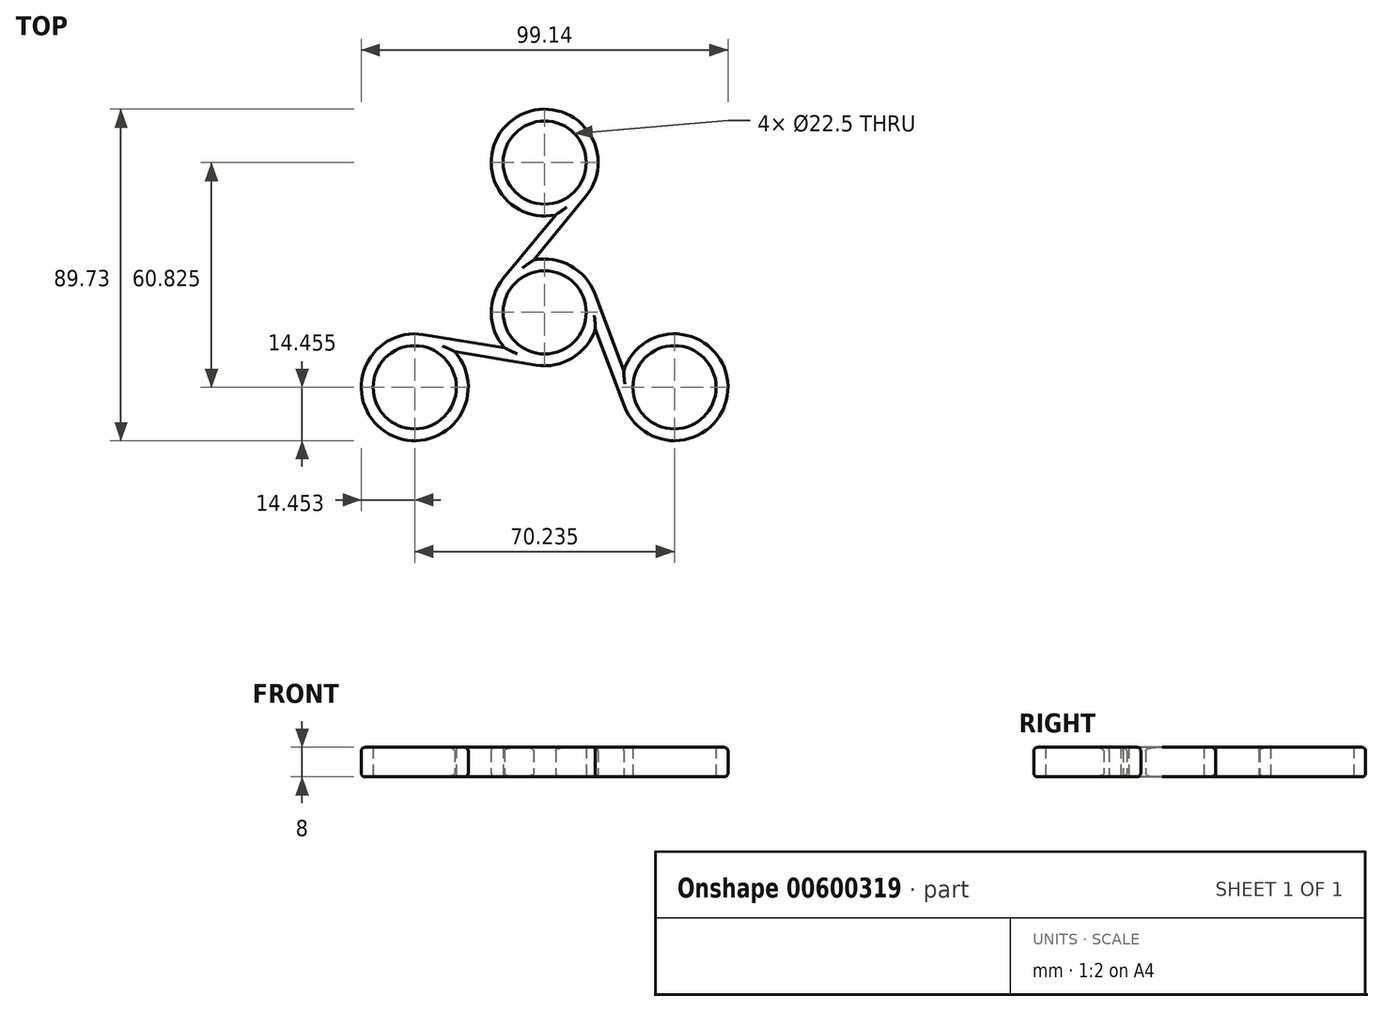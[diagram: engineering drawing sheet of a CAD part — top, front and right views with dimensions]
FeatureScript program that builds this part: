
annotation { "Feature Type Name" : "Feature", "Feature Type Description" : "" }
export const myFeature = defineFeature(function(context is Context, id is Id, definition is map)
    precondition{}
    {
        {
            var Q0;
            Q0=qCreatedBy(makeId("Top.planeOp"),FACE);
            var sketch = newSketch(context, id + "F0", { "sketchPlane" : qUnion([Q0])});
            skCircle(sketch, "E0", {"center": v(0, 0) * mm, "radius": 11.25 * mm});
            skLineSegment(sketch, "E1", {"start": v(0, 0) * mm, "end": v(0, 40.55) * mm, "construction": true});
            skLineSegment(sketch, "E2", {"start": v(-35.12, -20.27) * mm, "end": v(0, 0) * mm, "construction": true});
            skLineSegment(sketch, "E3", {"start": v(0, 0) * mm, "end": v(35.12, -20.27) * mm, "construction": true});
            skCircle(sketch, "E4", {"center": v(0, 40.55) * mm, "radius": 11.25 * mm});
            skCircle(sketch, "E5", {"center": v(35.12, -20.27) * mm, "radius": 11.25 * mm});
            skCircle(sketch, "E6", {"center": v(-35.12, -20.27) * mm, "radius": 11.25 * mm});
            skCircle(sketch, "E7", {"center": v(0, 0) * mm, "radius": 55 * mm, "construction": true});
            skCircle(sketch, "E8", {"center": v(0, 0) * mm, "radius": 14.45 * mm});
            skLineSegment(sketch, "E9", {"start": v(10.53, 3.97) * mm, "end": v(21.6, -25.38) * mm});
            skLineSegment(sketch, "E10", {"start": v(13.52, 5.1) * mm, "end": v(24.6, -24.25) * mm});
            skCircle(sketch, "E11", {"center": v(35.12, -20.27) * mm, "radius": 14.45 * mm});
            skCircle(sketch, "E12", {"center": v(0, 40.55) * mm, "radius": 14.45 * mm});
            skCircle(sketch, "E13", {"center": v(-35.12, -20.27) * mm, "radius": 14.45 * mm});
            skLineSegment(sketch, "E14", {"start": v(-1.82, -11.1) * mm, "end": v(-32.77, -6.02) * mm});
            skLineSegment(sketch, "E15", {"start": v(-2.34, -14.26) * mm, "end": v(-33.3, -9.17) * mm});
            skLineSegment(sketch, "E16", {"start": v(-11.18, 9.16) * mm, "end": v(8.7, 33.42) * mm});
            skLineSegment(sketch, "E17", {"start": v(11.18, 31.4) * mm, "end": v(-8.7, 7.13) * mm});
            skSolve(sketch);
        }
        {
            var Q0;
            Q0 = qSketchRegion(id + "F0", true);
            extrude(context, id + "F1", {"entities" : qUnion([Q0]), "endBound" : BoundingType.SYMMETRIC, "depth" : 8 * mm, "offsetDistance" : 25 * mm});
        }
        {
            var Q0;
            {var subQ0=sQuery(id+"F0.wireOp",EDGE,"E8");Q0=makeQuery(id+"F1.opExtrude","CAP_EDGE",EDGE,{"disambiguationData":[OSD([subQ0]),TDD([makeQuery(id+"F0.imprint","IMPRINT",EDGE,{"disambiguationData":[TD([[makeQuery(id+"F0.imprint","INTERSECT",VERTEX,{"derivedFrom":[subQ0,sQuery(id+"F0.wireOp",EDGE,"E10")]}),-1.0]])],"derivedFrom":subQ0})])],"isStart":false});}
            var Q1;
            Q1=makeQuery(id+"F1.opExtrude","CAP_EDGE",EDGE,{"disambiguationData":[OSD([sQuery(id+"F0.wireOp",EDGE,"E11")])],"isStart":false});
            var Q2;
            Q2=makeQuery(id+"F1.opExtrude","CAP_EDGE",EDGE,{"disambiguationData":[OSD([sQuery(id+"F0.wireOp",EDGE,"E12")])],"isStart":false});
            var Q3;
            Q3=makeQuery(id+"F1.opExtrude","CAP_EDGE",EDGE,{"disambiguationData":[OSD([sQuery(id+"F0.wireOp",EDGE,"E16")])],"isStart":false});
            var Q4;
            Q4=makeQuery(id+"F1.opExtrude","CAP_EDGE",EDGE,{"disambiguationData":[OSD([sQuery(id+"F0.wireOp",EDGE,"E13")])],"isStart":false});
            var Q5;
            {var subQ0=sQuery(id+"F0.wireOp",EDGE,"E8");Q5=makeQuery(id+"F1.opExtrude","CAP_EDGE",EDGE,{"disambiguationData":[OSD([subQ0]),TDD([makeQuery(id+"F0.imprint","IMPRINT",EDGE,{"disambiguationData":[TD([[makeQuery(id+"F0.imprint","INTERSECT",VERTEX,{"derivedFrom":[subQ0,sQuery(id+"F0.wireOp",EDGE,"E15")]}),-1.0]])],"derivedFrom":subQ0})])],"isStart":false});}
            var Q6;
            Q6=makeQuery(id+"F1.opExtrude","CAP_EDGE",EDGE,{"disambiguationData":[OSD([sQuery(id+"F0.wireOp",EDGE,"E15")])],"isStart":false});
            var Q7;
            Q7=makeQuery(id+"F1.opExtrude","CAP_EDGE",EDGE,{"disambiguationData":[OSD([sQuery(id+"F0.wireOp",EDGE,"E10")])],"isStart":false});
            var Q8;
            Q8=makeQuery(id+"F1.opExtrude","CAP_EDGE",EDGE,{"disambiguationData":[OSD([sQuery(id+"F0.wireOp",EDGE,"E14")])],"isStart":false});
            var Q9;
            {var subQ0=sQuery(id+"F0.wireOp",EDGE,"E8");Q9=makeQuery(id+"F1.opExtrude","CAP_EDGE",EDGE,{"disambiguationData":[OSD([subQ0]),TDD([makeQuery(id+"F0.imprint","IMPRINT",EDGE,{"disambiguationData":[TD([[makeQuery(id+"F0.imprint","INTERSECT",VERTEX,{"derivedFrom":[subQ0,sQuery(id+"F0.wireOp",EDGE,"E16")]}),-1.0]])],"derivedFrom":subQ0})])],"isStart":false});}
            var Q10;
            Q10=makeQuery(id+"F1.opExtrude","CAP_EDGE",EDGE,{"disambiguationData":[OSD([sQuery(id+"F0.wireOp",EDGE,"E13")])],"isStart":true});
            var Q11;
            {var subQ0=sQuery(id+"F0.wireOp",EDGE,"E8");Q11=makeQuery(id+"F1.opExtrude","CAP_EDGE",EDGE,{"disambiguationData":[OSD([subQ0]),TDD([makeQuery(id+"F0.imprint","IMPRINT",EDGE,{"disambiguationData":[TD([[makeQuery(id+"F0.imprint","INTERSECT",VERTEX,{"derivedFrom":[subQ0,sQuery(id+"F0.wireOp",EDGE,"E15")]}),-1.0]])],"derivedFrom":subQ0})])],"isStart":true});}
            var Q12;
            Q12=makeQuery(id+"F1.opExtrude","CAP_EDGE",EDGE,{"disambiguationData":[OSD([sQuery(id+"F0.wireOp",EDGE,"E11")])],"isStart":true});
            var Q13;
            {var subQ0=sQuery(id+"F0.wireOp",EDGE,"E8");Q13=makeQuery(id+"F1.opExtrude","CAP_EDGE",EDGE,{"disambiguationData":[OSD([subQ0]),TDD([makeQuery(id+"F0.imprint","IMPRINT",EDGE,{"disambiguationData":[TD([[makeQuery(id+"F0.imprint","INTERSECT",VERTEX,{"derivedFrom":[subQ0,sQuery(id+"F0.wireOp",EDGE,"E10")]}),-1.0]])],"derivedFrom":subQ0})])],"isStart":true});}
            var Q14;
            Q14=makeQuery(id+"F1.opExtrude","CAP_EDGE",EDGE,{"disambiguationData":[OSD([sQuery(id+"F0.wireOp",EDGE,"E16")])],"isStart":true});
            var Q15;
            Q15=makeQuery(id+"F1.opExtrude","CAP_EDGE",EDGE,{"disambiguationData":[OSD([sQuery(id+"F0.wireOp",EDGE,"E17")])],"isStart":true});
            fillet(context, id + "F2", {"entities" : qUnion([Q0, Q1, Q2, Q3, Q4, Q5, Q6, Q7, Q8, Q9, Q10, Q11, Q12, Q13, Q14, Q15]), "radius" : 1 * mm, "tangentPropagation" : true, "allowEdgeOverflow" : false});
        }
    });
